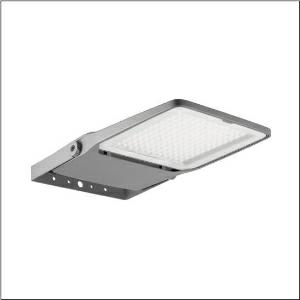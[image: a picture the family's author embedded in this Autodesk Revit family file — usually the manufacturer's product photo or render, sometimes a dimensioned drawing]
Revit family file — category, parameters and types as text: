
# Revit family: floodlight_fl_20_midi___pl61_5xa7682d3c2ac_39fc
name_source: partatom
category: Lighting Fixtures
units: mm (PartAtom-declared; Revit-internal decimal feet)

## family parameters
Cut with Voids When Loaded = No
Host = Face
Light Source = No
Part Type = Normal
Room Calculation Point = No
Round Connector Dimension = Use Diameter
Shared = No

## types (1)
- --- (1 x LED 5000K / CRI = 70 (unbekannt), 18470 lm, 5000K)
    Apparent Load = 142 VA
    CIE Flux Codes = 33 65 98 100 100
    Color Rendering = 70
    Color Temperature = 5000K
    Default Elevation = 1800 mm
    Description = Floodlight FL 20 midi, floodlight, primary light control with lens, of plastic, primary optical cover: protective disc, of toughened safety glass, transparent, light distribution: PL61, light emission: direct distribution, primary light characteristic: asymmetric, installation type: surface-mounted, LED High Power LED, rated luminous flux: 18.470 lm, light colour: 750, colour temperature: 5000K, control gear: ECG Plus, control: digital communication interface, time-dependent luminous flux control, flexible luminous flux parameterisation, power reduction, overheat protection, electronic power reduction, with terminal, 5-pole, max. 2.5mm², mains connection: 220..240V, AC, 50/60Hz, rated input power: 142W, LED unit, of diecast aluminium, powder-coated, Siteco® metallic grey (DB 702S), length: 731 mm, width: 450 mm, height: 76mm, housing frame, of diecast aluminium, powder-coated, Siteco® metallic grey (DB 702S), wall fastening, of steel, powder-coated, Siteco® metallic grey (DB 702S), DALIprotection rating (complete): IP66, insulation class (complete): insulation class II (safety insulation), certification: CE, ENEC, VDE, protection symbol: D, permissible ambient temperature for indoor applications: -40..+40°C, permissible ambient temperature for outdoor applications: -40..+50°C, standard: DIN EN 12944, packaging unit: 1 piece

Light Distribution: PL61
    Height = 76 mm
    Lamp = 1 x LED 5000K / CRI >= 70 (unbekannt)
    Lamp Light Flux = 18470 lm
    Lamp count = 1
    Length = 731 mm
    Luminous efficacy = 130 lm/W
    Manufacturer = Siteco
    ModVariant = No
    Model = 5XA7682D3C2AC
    Number of Poles = 1
    OnlyDefault = Yes
    Power Factor = 1
    Product Name = Floodlight FL 20 midi | PL61
    Product group = floodlight | pylon top
    ProductGroupID = 6101
    Protection Class = Protection class II
    Protection Degree = IP 66
    RLX_Detail_Level = 1
    RlxData = <blob elided: 91797 chars, md5=e08d410e>
    Socket = socket
    Standby Power = 0 W
    System Light Flux = 18470 lm
    System Power = 142 W
    Type Comments = factory setting: luminous flux: 100 % | dim-lin: 254 | 489 mA
    Type Image = l_1005944.jpg
    URL = http://relux.com
    VarID = @adj_142499
    Voltage = 0 V
    Weight = 0.00 kg
    Width = 450 mm

## geometry (parser evidence)
native form markers: Blend x4, Sweep x13
no freeform markers — native parametric forms only
